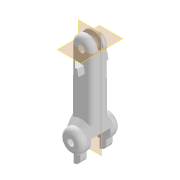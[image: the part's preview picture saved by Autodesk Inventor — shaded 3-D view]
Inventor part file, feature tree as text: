
AUTODESK INVENTOR PART (.ipt)
format: ipt  version: 2020.2 (Build 242310000, 310)  size: 317,440 bytes
history: native  units: mm
features: sketch x9, extrude x8, mirror x5, chamfer x3, fillet x3, plane x2, revolve x1
ambient origin geometry x8: Origin, YZ Plane, XZ Plane, XY Plane, X Axis, Y Axis, Z Axis, Center Point
bodies: Solid1 (feature_tree)
feature tree (31):
  extrude  "base"  Depth=35.0mm
  extrude  "joint"  Depth=10.0mm
  plane  "Work Plane1"
  mirror  "Mirror1"
  chamfer  "Chamfer1"  Distance=8.0mm
  extrude  "joint_2"  Depth=3.0mm
  fillet  "Fillet2"  Radius=5.0mm
  plane  "Work Plane2"
  revolve  "Revolution2"  [1 undecoded]
  extrude  "Extrusion8"  Depth=2.0mm TaperAngle=45.0deg
  extrude  "Extrusion9"  Depth=2.0mm
  mirror  "Mirror4"
  fillet  "Fillet4"  Radius=3.5mm
  extrude  "Extrusion10"  Depth=40.0mm TaperAngle=0.0deg
  mirror  "Mirror5"
  chamfer  "Chamfer3"  Distance=13.962634mm
  extrude  "lock_1"  Depth=2.0mm
  mirror  "Mirror2"
  chamfer  "Chamfer2"  Distance=3.0mm
  extrude  "lock_2"  Depth=3.0mm TaperAngle=45.0deg
  mirror  "Mirror3"
  fillet  "Fillet3"  Radius=4.0mm
  sketch  "Sketch1"  dims[d0=3.0mm d1=35.0mm]
  sketch  "Sketch2"  dims[d2=3.0mm d3=10.0mm]
  sketch  "Sketch4"  dims[d4=10.0mm d5=8.0mm d6=0.0mm]
  sketch  "Sketch7"  dims[d7=10.0mm d8=3.0mm d9=5.0mm d10=0.0mm]
  sketch  "Sketch8"  dims[d12=10.5mm d13=3.0mm]
  sketch  "Sketch9"  dims[d14=9.0mm d15=0.0mm d16=2.0mm d17=2.0mm d18=45.0deg]
  sketch  "Sketch10"  dims[d19=2.0mm d20=3.5mm d21=3.5mm]
  sketch  "Sketch11"  dims[d23=2.5mm d24=40.0mm d25=0.0mm]
  sketch  "Sketch12"  dims[d32=6.0mm d33=13.962634mm d34=5.0mm d35=3.0mm d36=0.0mm d37=3.0mm d38=2.0mm d39=45.0deg d40=4.0mm d41=3.0mm d42=3.0mm d43=0.0mm d44=3.0mm d45=4.0mm d46=90.0deg d47=3.5mm d48=2.5mm d49=180.0deg d50=5.0mm d51=0.0mm d52=4.0mm d53=3.0mm d54=3.0mm d55=0.0mm d56=3.0mm d57=6.0mm d58=3.0mm d59=13.962634mm d60=3.0mm d61=0.0mm d62=3.0mm d63=2.0mm d64=45.0deg]
note: 1 required parameter value undecoded (feature->parameter linkage not recoverable at this tier; creation-order binding heuristic only, values carry confidence <= 0.55)
